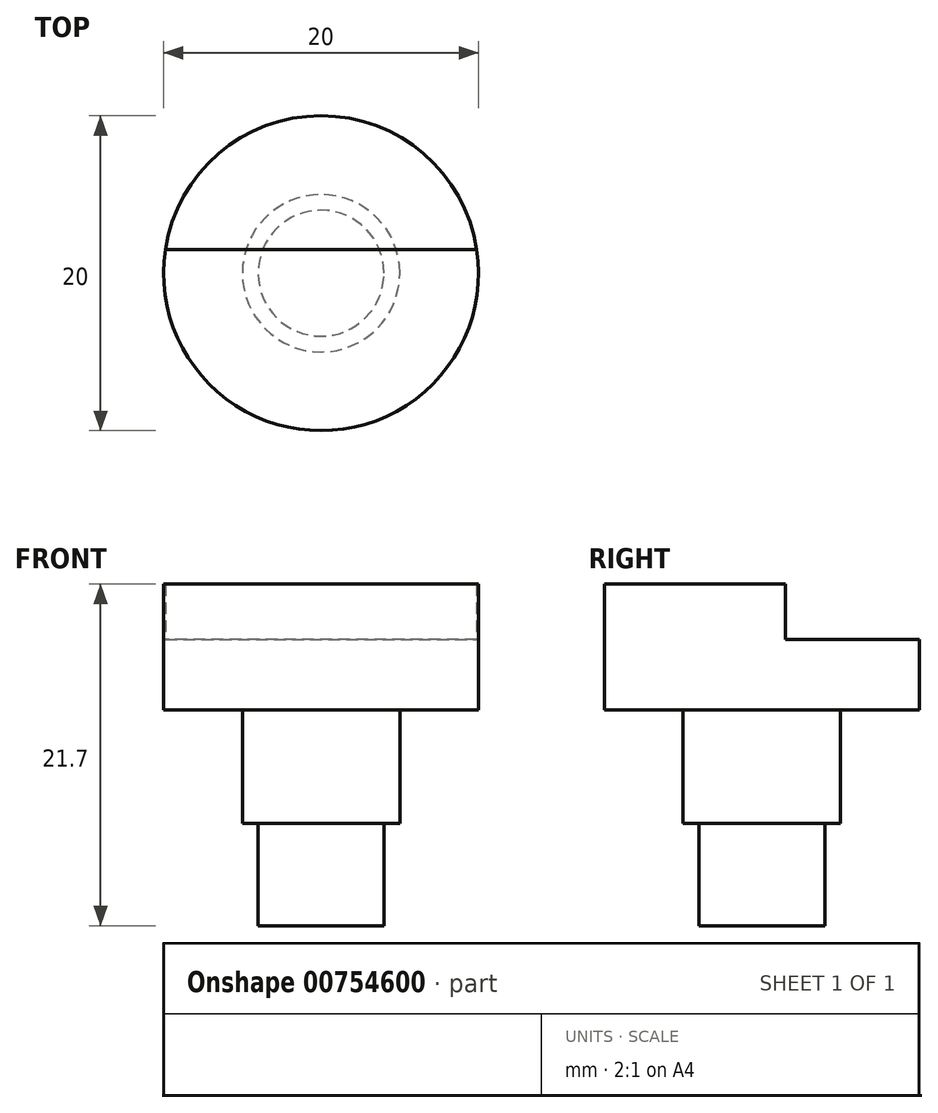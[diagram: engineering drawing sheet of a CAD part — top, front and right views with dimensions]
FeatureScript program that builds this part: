
annotation { "Feature Type Name" : "Feature", "Feature Type Description" : "" }
export const myFeature = defineFeature(function(context is Context, id is Id, definition is map)
    precondition{}
    {
        {
            var Q0;
            Q0=qCreatedBy(makeId("Top.planeOp"),FACE);
            var sketch = newSketch(context, id + "F0", { "sketchPlane" : qUnion([Q0])});
            skCircle(sketch, "E0", {"center": v(0, 0) * mm, "radius": 4 * mm});
            skSolve(sketch);
        }
        {
            var Q0;
            Q0 = qSketchRegion(id + "F0", true);
            extrude(context, id + "F1", {"entities" : qUnion([Q0]), "depth" : 6.5 * mm, "offsetDistance" : 25 * mm});
        }
        {
            var Q0;
            Q0=makeQuery(id+"F1.opExtrude","CAP_FACE",FACE,{"disambiguationData":[OSD([sQuery(id+"F0.wireOp",EDGE,"E0")])],"isStart":false});
            var sketch = newSketch(context, id + "F2", { "sketchPlane" : qUnion([Q0])});
            skCircle(sketch, "E1", {"center": v(0, 0) * mm, "radius": 5 * mm});
            skSolve(sketch);
        }
        {
            var Q0;
            Q0 = qSketchRegion(id + "F2", true);
            extrude(context, id + "F3", {"entities" : qUnion([Q0]), "operationType" : NewBodyOperationType.ADD, "depth" : 7.2 * mm, "offsetDistance" : 25 * mm});
        }
        {
            var Q0;
            Q0=makeQuery(id+"F3.opExtrude","CAP_FACE",FACE,{"disambiguationData":[OSD([sQuery(id+"F2.wireOp",EDGE,"E1")])],"isStart":false});
            var sketch = newSketch(context, id + "F4", { "sketchPlane" : qUnion([Q0])});
            skCircle(sketch, "E2", {"center": v(0, 0) * mm, "radius": 10 * mm});
            skSolve(sketch);
        }
        {
            var Q0;
            Q0 = qSketchRegion(id + "F4", true);
            extrude(context, id + "F5", {"entities" : qUnion([Q0]), "operationType" : NewBodyOperationType.ADD, "depth" : 4.5 * mm, "offsetDistance" : 25 * mm});
        }
        {
            var Q0;
            Q0=makeQuery(id+"F5.opExtrude","CAP_FACE",FACE,{"disambiguationData":[OSD([sQuery(id+"F4.wireOp",EDGE,"E2")])],"isStart":false});
            var sketch = newSketch(context, id + "F6", { "sketchPlane" : qUnion([Q0])});
            skCircle(sketch, "E3", {"center": v(0, 0) * mm, "radius": 10 * mm});
            skPoint(sketch, "E4", {"position": v(-10, 0) * mm});
            skPoint(sketch, "E5", {"position": v(10, 0) * mm});
            skLineSegment(sketch, "E6.bottom", {"start": v(-10, -1.5) * mm, "end": v(10, -1.5) * mm});
            skLineSegment(sketch, "E6.top", {"start": v(-10, 1.5) * mm, "end": v(10, 1.5) * mm});
            skLineSegment(sketch, "E6.left", {"start": v(-10, -1.5) * mm, "end": v(-10, 1.5) * mm});
            skLineSegment(sketch, "E6.right", {"start": v(10, -1.5) * mm, "end": v(10, 1.5) * mm});
            skSolve(sketch);
        }
        {
            var Q0;
            {var subQ0=sQuery(id+"F6.wireOp",EDGE,"E6.bottom");var subQ1=sQuery(id+"F6.wireOp",EDGE,"E3");var subQ2=makeQuery(id+"F6.imprint","INTERSECT",VERTEX,{"disambiguationData":[OD(0.0)],"derivedFrom":[subQ1,subQ0]});Q0=makeQuery(id+"F6.imprint","IMPRINT",FACE,{"disambiguationData":[TD([[makeQuery(id+"F6.imprint","IMPRINT",EDGE,{"disambiguationData":[TD([[subQ2,-1.0]])],"derivedFrom":subQ1}),1.0]])]});}
            var Q1;
            {var subQ0=sQuery(id+"F6.wireOp",EDGE,"E6.top");var subQ1=sQuery(id+"F6.wireOp",EDGE,"E3");var subQ2=makeQuery(id+"F6.imprint","INTERSECT",VERTEX,{"disambiguationData":[OD(0.0)],"derivedFrom":[subQ1,subQ0]});Q1=makeQuery(id+"F6.imprint","IMPRINT",FACE,{"disambiguationData":[TD([[makeQuery(id+"F6.imprint","IMPRINT",EDGE,{"disambiguationData":[TD([[subQ2,-1.0]])],"derivedFrom":subQ1}),1.0]])]});}
            extrude(context, id + "F7", {"entities" : qUnion([Q0, Q1]), "operationType" : NewBodyOperationType.ADD, "depth" : 3.5 * mm, "offsetDistance" : 25 * mm});
        }
    });
